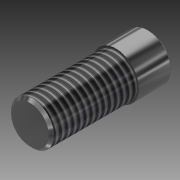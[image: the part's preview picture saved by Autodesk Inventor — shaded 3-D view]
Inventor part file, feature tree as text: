
AUTODESK INVENTOR PART (.ipt)
format: ipt  version: 2013 (Build 170138000, 138)  size: 124,416 bytes
history: native  units: mm (DEFAULTED — no unit token found)
features: extrude x2, chamfer x2, sketch x2, thread x1, reference x1
ambient origin geometry x8: Origin, YZ Plane, XZ Plane, XY Plane, X Axis, Y Axis, Z Axis, Center Point
bodies: Solid1 (feature_tree)
feature tree (8):
  extrude  "Extrusion1"  Depth=5.08mm TaperAngle=0.0deg
  chamfer  "Chamfer1"  Distance=0.381mm
  extrude  "Extrusion2"  Depth=12.7mm TaperAngle=0.0deg
  chamfer  "Chamfer2"  Distance=0.381mm
  thread  "Thread1"  [1 undecoded]
  sketch  "Sketch1"  dims[d0=6.858mm d1=5.08mm d2=0.0mm d3=0.381mm d4=3.175mm]
  reference  "Reference1"
  sketch  "Sketch2"  dims[d5=6.35mm d6=12.7mm d7=0.0mm d8=0.381mm d9=3.175mm d10=25.4mm d11=0.0mm d12=45.0deg d13=45.0deg]
note: 1 required parameter value undecoded (feature->parameter linkage not recoverable at this tier; creation-order binding heuristic only, values carry confidence <= 0.55)
